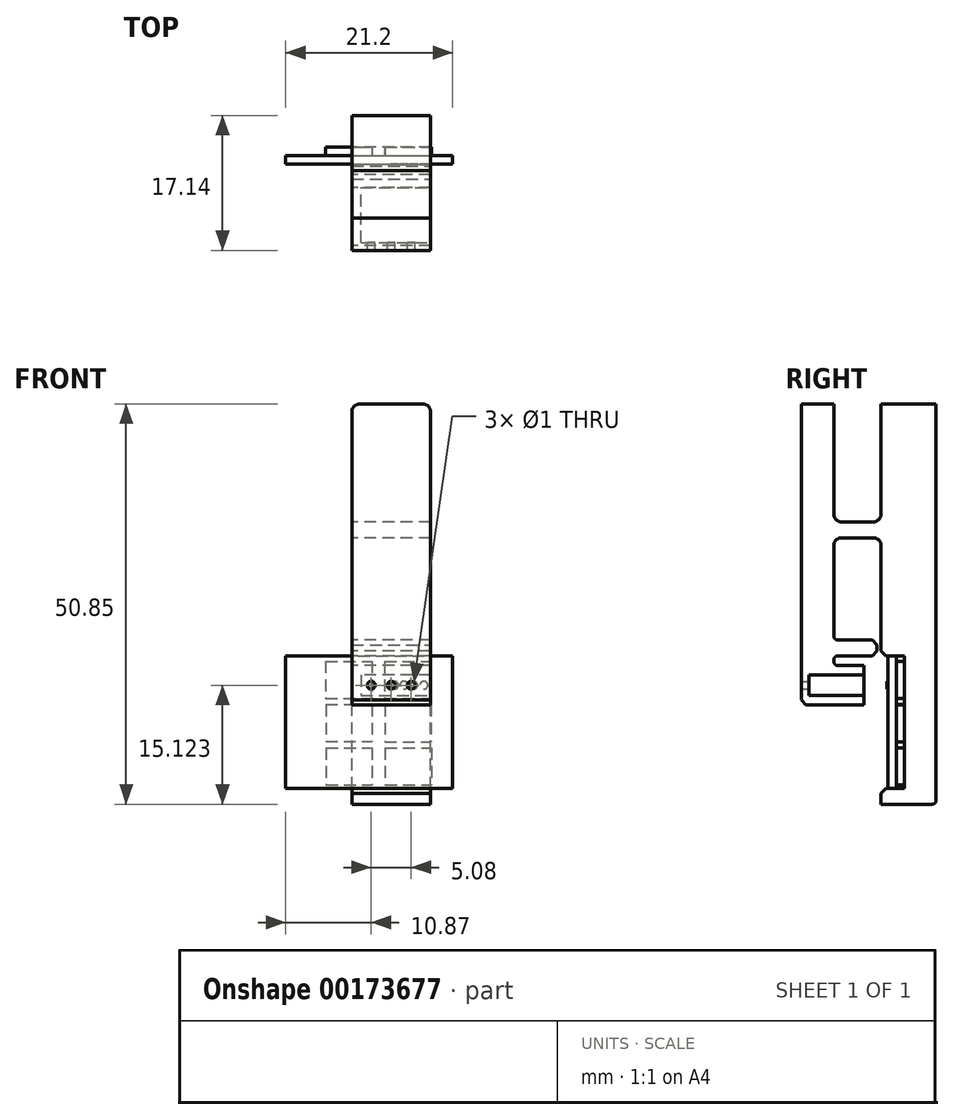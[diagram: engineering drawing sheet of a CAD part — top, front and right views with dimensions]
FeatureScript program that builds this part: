
annotation { "Feature Type Name" : "Feature", "Feature Type Description" : "" }
export const myFeature = defineFeature(function(context is Context, id is Id, definition is map)
    precondition{}
    {
        {
            var Q0;
            Q0=qCreatedBy(makeId("Front.planeOp"),FACE);
            var sketch = newSketch(context, id + "F0", { "sketchPlane" : qUnion([Q0])});
            skLineSegment(sketch, "E0.bottom", {"start": v(-8.41, 12.67) * mm, "end": v(12.79, 12.67) * mm});
            skLineSegment(sketch, "E0.top", {"start": v(-8.41, -4.18) * mm, "end": v(12.79, -4.18) * mm});
            skLineSegment(sketch, "E0.left", {"start": v(-8.41, 12.67) * mm, "end": v(-8.41, -4.18) * mm});
            skLineSegment(sketch, "E0.right", {"start": v(12.79, 12.67) * mm, "end": v(12.79, -4.18) * mm});
            skCircle(sketch, "E1", {"center": v(9.15, 8.94) * mm, "radius": 0.5 * mm});
            skCircle(sketch, "E2", {"center": v(7.85, 8.94) * mm, "radius": 0.5 * mm});
            skCircle(sketch, "E3", {"center": v(6.63, 8.94) * mm, "radius": 0.5 * mm});
            skCircle(sketch, "E4", {"center": v(5.4, 8.94) * mm, "radius": 0.5 * mm});
            skLineSegment(sketch, "E5.bottom", {"start": v(4.22, 0.96) * mm, "end": v(10.09, 0.96) * mm});
            skLineSegment(sketch, "E5.top", {"start": v(4.22, -3.74) * mm, "end": v(10.09, -3.74) * mm});
            skLineSegment(sketch, "E5.left", {"start": v(4.22, 0.96) * mm, "end": v(4.22, -3.74) * mm});
            skLineSegment(sketch, "E5.right", {"start": v(10.09, 0.96) * mm, "end": v(10.09, -3.74) * mm});
            skLineSegment(sketch, "E6.0.1.0", {"start": v(10.06, 6.46) * mm, "end": v(10.06, 1.76) * mm});
            skLineSegment(sketch, "E6.0.1.1", {"start": v(4.19, 6.46) * mm, "end": v(10.06, 6.46) * mm});
            skLineSegment(sketch, "E6.0.1.2", {"start": v(4.19, 6.46) * mm, "end": v(4.19, 1.76) * mm});
            skLineSegment(sketch, "E6.0.1.3", {"start": v(4.19, 1.76) * mm, "end": v(10.06, 1.76) * mm});
            skLineSegment(sketch, "E6.0.2.0", {"start": v(10.03, 11.96) * mm, "end": v(10.03, 7.26) * mm});
            skLineSegment(sketch, "E6.0.2.1", {"start": v(4.16, 11.96) * mm, "end": v(10.03, 11.96) * mm});
            skLineSegment(sketch, "E6.0.2.2", {"start": v(4.16, 11.96) * mm, "end": v(4.16, 7.26) * mm});
            skLineSegment(sketch, "E6.0.2.3", {"start": v(4.16, 7.26) * mm, "end": v(10.03, 7.26) * mm});
            skLineSegment(sketch, "E6.1.0.0", {"start": v(2.59, 0.98) * mm, "end": v(2.59, -3.72) * mm});
            skLineSegment(sketch, "E6.1.0.1", {"start": v(-3.28, 0.98) * mm, "end": v(2.59, 0.98) * mm});
            skLineSegment(sketch, "E6.1.0.2", {"start": v(-3.28, 0.98) * mm, "end": v(-3.28, -3.72) * mm});
            skLineSegment(sketch, "E6.1.0.3", {"start": v(-3.28, -3.72) * mm, "end": v(2.59, -3.72) * mm});
            skLineSegment(sketch, "E6.1.1.0", {"start": v(2.56, 6.48) * mm, "end": v(2.56, 1.78) * mm});
            skLineSegment(sketch, "E6.1.1.1", {"start": v(-3.31, 6.48) * mm, "end": v(2.56, 6.48) * mm});
            skLineSegment(sketch, "E6.1.1.2", {"start": v(-3.31, 6.48) * mm, "end": v(-3.31, 1.78) * mm});
            skLineSegment(sketch, "E6.1.1.3", {"start": v(-3.31, 1.78) * mm, "end": v(2.56, 1.78) * mm});
            skLineSegment(sketch, "E6.1.2.0", {"start": v(2.53, 11.98) * mm, "end": v(2.53, 7.28) * mm});
            skLineSegment(sketch, "E6.1.2.1", {"start": v(-3.34, 11.98) * mm, "end": v(2.53, 11.98) * mm});
            skLineSegment(sketch, "E6.1.2.2", {"start": v(-3.34, 11.98) * mm, "end": v(-3.34, 7.28) * mm});
            skLineSegment(sketch, "E6.1.2.3", {"start": v(-3.34, 7.28) * mm, "end": v(2.53, 7.28) * mm});
            skLineSegment(sketch, "E6.direction1", {"start": v(4.22, -3.74) * mm, "end": v(-3.28, -3.72) * mm, "construction": true});
            skLineSegment(sketch, "E6.direction2", {"start": v(4.22, -3.74) * mm, "end": v(4.19, 1.76) * mm, "construction": true});
            skSolve(sketch);
        }
        {
            var Q0;
            Q0=makeQuery(id+"F0.imprint","IMPRINT",FACE,{"disambiguationData":[TD([[makeQuery(id+"F0.imprint","IMPRINT",EDGE,{"derivedFrom":sQuery(id+"F0.wireOp",EDGE,"E0.bottom")}),-1.0]])]});
            var Q1;
            Q1=makeQuery(id+"F0.imprint","IMPRINT",FACE,{"disambiguationData":[TD([[makeQuery(id+"F0.imprint","IMPRINT",EDGE,{"derivedFrom":sQuery(id+"F0.wireOp",EDGE,"E6.1.2.0")}),-1.0]])]});
            var Q2;
            Q2=makeQuery(id+"F0.imprint","IMPRINT",FACE,{"disambiguationData":[TD([[makeQuery(id+"F0.imprint","IMPRINT",EDGE,{"derivedFrom":sQuery(id+"F0.wireOp",EDGE,"E1")}),-1.0]])]});
            var Q3;
            Q3=makeQuery(id+"F0.imprint","IMPRINT",FACE,{"disambiguationData":[TD([[makeQuery(id+"F0.imprint","IMPRINT",EDGE,{"derivedFrom":sQuery(id+"F0.wireOp",EDGE,"E6.1.1.0")}),-1.0]])]});
            var Q4;
            Q4=makeQuery(id+"F0.imprint","IMPRINT",FACE,{"disambiguationData":[TD([[makeQuery(id+"F0.imprint","IMPRINT",EDGE,{"derivedFrom":sQuery(id+"F0.wireOp",EDGE,"E6.0.1.0")}),-1.0]])]});
            var Q5;
            Q5=makeQuery(id+"F0.imprint","IMPRINT",FACE,{"disambiguationData":[TD([[makeQuery(id+"F0.imprint","IMPRINT",EDGE,{"derivedFrom":sQuery(id+"F0.wireOp",EDGE,"E6.1.0.0")}),-1.0]])]});
            var Q6;
            Q6=makeQuery(id+"F0.imprint","IMPRINT",FACE,{"disambiguationData":[TD([[makeQuery(id+"F0.imprint","IMPRINT",EDGE,{"derivedFrom":sQuery(id+"F0.wireOp",EDGE,"E5.bottom")}),-1.0]])]});
            extrude(context, id + "F1", {"entities" : qUnion([Q0, Q1, Q2, Q3, Q4, Q5, Q6]), "oppositeDirection" : true, "depth" : 1.08 * mm});
        }
        {
            var Q0;
            Q0=makeQuery(id+"F0.imprint","IMPRINT",FACE,{"disambiguationData":[TD([[makeQuery(id+"F0.imprint","IMPRINT",EDGE,{"derivedFrom":sQuery(id+"F0.wireOp",EDGE,"E6.1.0.0")}),-1.0]])]});
            var Q1;
            Q1=makeQuery(id+"F0.imprint","IMPRINT",FACE,{"disambiguationData":[TD([[makeQuery(id+"F0.imprint","IMPRINT",EDGE,{"derivedFrom":sQuery(id+"F0.wireOp",EDGE,"E6.1.1.0")}),-1.0]])]});
            var Q2;
            Q2=makeQuery(id+"F0.imprint","IMPRINT",FACE,{"disambiguationData":[TD([[makeQuery(id+"F0.imprint","IMPRINT",EDGE,{"derivedFrom":sQuery(id+"F0.wireOp",EDGE,"E6.1.2.0")}),-1.0]])]});
            var Q3;
            Q3=makeQuery(id+"F0.imprint","IMPRINT",FACE,{"disambiguationData":[TD([[makeQuery(id+"F0.imprint","IMPRINT",EDGE,{"derivedFrom":sQuery(id+"F0.wireOp",EDGE,"E5.bottom")}),-1.0]])]});
            var Q4;
            Q4=makeQuery(id+"F0.imprint","IMPRINT",FACE,{"disambiguationData":[TD([[makeQuery(id+"F0.imprint","IMPRINT",EDGE,{"derivedFrom":sQuery(id+"F0.wireOp",EDGE,"E6.0.1.0")}),-1.0]])]});
            var Q5;
            Q5=makeQuery(id+"F0.imprint","IMPRINT",FACE,{"disambiguationData":[TD([[makeQuery(id+"F0.imprint","IMPRINT",EDGE,{"derivedFrom":sQuery(id+"F0.wireOp",EDGE,"E1")}),-1.0]])]});
            var Q6;
            Q6=makeQuery(id+"F0.imprint","IMPRINT",FACE,{"disambiguationData":[TD([[makeQuery(id+"F0.imprint","IMPRINT",EDGE,{"derivedFrom":sQuery(id+"F0.wireOp",EDGE,"E4")}),1.0]])]});
            var Q7;
            Q7=makeQuery(id+"F0.imprint","IMPRINT",FACE,{"disambiguationData":[TD([[makeQuery(id+"F0.imprint","IMPRINT",EDGE,{"derivedFrom":sQuery(id+"F0.wireOp",EDGE,"E3")}),1.0]])]});
            var Q8;
            Q8=makeQuery(id+"F0.imprint","IMPRINT",FACE,{"disambiguationData":[TD([[makeQuery(id+"F0.imprint","IMPRINT",EDGE,{"derivedFrom":sQuery(id+"F0.wireOp",EDGE,"E2")}),1.0]])]});
            var Q9;
            Q9=makeQuery(id+"F0.imprint","IMPRINT",FACE,{"disambiguationData":[TD([[makeQuery(id+"F0.imprint","IMPRINT",EDGE,{"derivedFrom":sQuery(id+"F0.wireOp",EDGE,"E1")}),1.0]])]});
            extrude(context, id + "F2", {"entities" : qUnion([Q0, Q1, Q2, Q3, Q4, Q5, Q6, Q7, Q8, Q9]), "operationType" : NewBodyOperationType.ADD, "oppositeDirection" : true, "depth" : 2.14 * mm});
        }
        {
            var Q0;
            Q0=makeQuery(id+"F0.imprint","IMPRINT",FACE,{"disambiguationData":[TD([[makeQuery(id+"F0.imprint","IMPRINT",EDGE,{"derivedFrom":sQuery(id+"F0.wireOp",EDGE,"E4")}),1.0]])]});
            var Q1;
            Q1=makeQuery(id+"F0.imprint","IMPRINT",FACE,{"disambiguationData":[TD([[makeQuery(id+"F0.imprint","IMPRINT",EDGE,{"derivedFrom":sQuery(id+"F0.wireOp",EDGE,"E3")}),1.0]])]});
            var Q2;
            Q2=makeQuery(id+"F0.imprint","IMPRINT",FACE,{"disambiguationData":[TD([[makeQuery(id+"F0.imprint","IMPRINT",EDGE,{"derivedFrom":sQuery(id+"F0.wireOp",EDGE,"E2")}),1.0]])]});
            var Q3;
            Q3=makeQuery(id+"F0.imprint","IMPRINT",FACE,{"disambiguationData":[TD([[makeQuery(id+"F0.imprint","IMPRINT",EDGE,{"derivedFrom":sQuery(id+"F0.wireOp",EDGE,"E1")}),1.0]])]});
            extrude(context, id + "F3", {"entities" : qUnion([Q0, Q1, Q2, Q3]), "operationType" : NewBodyOperationType.ADD, "depth" : 0.1 * mm});
        }
        {
            var Q0;
            Q0=qCreatedBy(makeId("Right.planeOp"),FACE);
            var sketch = newSketch(context, id + "F4", { "sketchPlane" : qUnion([Q0])});
            skPoint(sketch, "E7.0", {"position": v(0, 8.94) * mm});
            skLineSegment(sketch, "E8.0", {"start": v(2.14, 11.98) * mm, "end": v(2.14, 7.28) * mm});
            skLineSegment(sketch, "E9.0", {"start": v(1.08, 12.67) * mm, "end": v(0, 12.67) * mm});
            skPoint(sketch, "E10.0", {"position": v(1.08, -4.18) * mm});
            skLineSegment(sketch, "E11", {"start": v(-0.86, -4.18) * mm, "end": v(2.14, -4.18) * mm});
            skLineSegment(sketch, "E12", {"start": v(2.14, -4.18) * mm, "end": v(2.14, 12.67) * mm});
            skLineSegment(sketch, "E13", {"start": v(2.14, 12.67) * mm, "end": v(-0.86, 12.67) * mm});
            skLineSegment(sketch, "E14", {"start": v(-0.86, 12.67) * mm, "end": v(-0.86, 27.67) * mm});
            skLineSegment(sketch, "E15", {"start": v(-0.86, 27.67) * mm, "end": v(-6.86, 27.67) * mm});
            skLineSegment(sketch, "E16", {"start": v(-6.86, 27.67) * mm, "end": v(-6.86, 14.67) * mm});
            skLineSegment(sketch, "E17", {"start": v(-6.86, 14.67) * mm, "end": v(-1.36, 14.67) * mm});
            skLineSegment(sketch, "E18", {"start": v(-1.36, 14.67) * mm, "end": v(-1.36, 12.67) * mm});
            skLineSegment(sketch, "E19", {"start": v(-1.36, 12.67) * mm, "end": v(-6.86, 12.67) * mm});
            skLineSegment(sketch, "E20", {"start": v(-6.86, 12.67) * mm, "end": v(-6.86, 11.44) * mm});
            skLineSegment(sketch, "E21", {"start": v(-6.86, 11.44) * mm, "end": v(-3, 11.44) * mm});
            skLineSegment(sketch, "E22", {"start": v(-3, 11.44) * mm, "end": v(-3, 6.44) * mm});
            skLineSegment(sketch, "E23", {"start": v(-3, 6.44) * mm, "end": v(-11, 6.44) * mm});
            skLineSegment(sketch, "E24", {"start": v(-11, 6.44) * mm, "end": v(-11, 44.67) * mm});
            skLineSegment(sketch, "E25", {"start": v(-11, 44.67) * mm, "end": v(-6.86, 44.67) * mm});
            skLineSegment(sketch, "E26", {"start": v(-6.86, 44.67) * mm, "end": v(-6.86, 29.67) * mm});
            skLineSegment(sketch, "E27", {"start": v(-6.86, 29.67) * mm, "end": v(-0.86, 29.67) * mm});
            skLineSegment(sketch, "E28", {"start": v(-0.86, 29.67) * mm, "end": v(-0.86, 44.67) * mm});
            skLineSegment(sketch, "E29", {"start": v(-0.86, 44.67) * mm, "end": v(6.14, 44.67) * mm});
            skLineSegment(sketch, "E30", {"start": v(6.14, 44.67) * mm, "end": v(6.14, -6.18) * mm});
            skLineSegment(sketch, "E31", {"start": v(6.14, -6.18) * mm, "end": v(-0.86, -6.18) * mm});
            skLineSegment(sketch, "E32", {"start": v(-0.86, -6.18) * mm, "end": v(-0.86, -4.18) * mm});
            skLineSegment(sketch, "E33", {"start": v(0, 8.94) * mm, "end": v(-3, 8.94) * mm, "construction": true});
            skSolve(sketch);
        }
        {
            var Q0;
            Q0 = qSketchRegion(id + "F4", true);
            extrude(context, id + "F5", {"entities" : qUnion([Q0]), "depth" : 10 * mm});
        }
        {
            var Q0;
            Q0=makeQuery(id+"F5.opExtrude","SWEPT_FACE",FACE,{"disambiguationData":[OSD([sQuery(id+"F4.wireOp",EDGE,"E22")])]});
            var sketch = newSketch(context, id + "F6", { "sketchPlane" : qUnion([Q0])});
            skLineSegment(sketch, "E34", {"start": v(-10, 8.94) * mm, "end": v(0, 8.94) * mm, "construction": true});
            skLineSegment(sketch, "E35", {"start": v(-5, 6.44) * mm, "end": v(-5, 11.44) * mm, "construction": true});
            skLineSegment(sketch, "E36.bottom", {"start": v(-1.14, 10.22) * mm, "end": v(-8.86, 10.22) * mm});
            skLineSegment(sketch, "E36.top", {"start": v(-1.14, 7.67) * mm, "end": v(-8.86, 7.67) * mm});
            skLineSegment(sketch, "E36.left", {"start": v(-1.14, 10.22) * mm, "end": v(-1.14, 7.67) * mm});
            skLineSegment(sketch, "E36.right", {"start": v(-8.86, 10.22) * mm, "end": v(-8.86, 7.67) * mm});
            skPoint(sketch, "E36.middle", {"position": v(-5, 8.94) * mm});
            skCircle(sketch, "E37", {"center": v(-5, 8.94) * mm, "radius": 0.5 * mm});
            skCircle(sketch, "E38", {"center": v(-7.54, 8.94) * mm, "radius": 0.5 * mm});
            skCircle(sketch, "E39", {"center": v(-2.46, 8.94) * mm, "radius": 0.5 * mm});
            skLineSegment(sketch, "E40", {"start": v(-8.86, 7.67) * mm, "end": v(-10, 7.67) * mm});
            skLineSegment(sketch, "E41", {"start": v(-10, 7.67) * mm, "end": v(-10, 10.22) * mm});
            skLineSegment(sketch, "E42", {"start": v(-10, 10.22) * mm, "end": v(-8.86, 10.22) * mm});
            skSolve(sketch);
        }
        {
            var Q0;
            Q0 = qSketchRegion(id + "F6", true);
            var Q1;
            Q1=makeQuery(id+"F6.imprint","IMPRINT",FACE,{"disambiguationData":[TD([[makeQuery(id+"F6.imprint","IMPRINT",EDGE,{"derivedFrom":sQuery(id+"F6.wireOp",EDGE,"E38")}),1.0]])]});
            var Q2;
            Q2=makeQuery(id+"F6.imprint","IMPRINT",FACE,{"disambiguationData":[TD([[makeQuery(id+"F6.imprint","IMPRINT",EDGE,{"derivedFrom":sQuery(id+"F6.wireOp",EDGE,"E37")}),1.0]])]});
            var Q3;
            Q3=makeQuery(id+"F6.imprint","IMPRINT",FACE,{"disambiguationData":[TD([[makeQuery(id+"F6.imprint","IMPRINT",EDGE,{"derivedFrom":sQuery(id+"F6.wireOp",EDGE,"E39")}),1.0]])]});
            extrude(context, id + "F7", {"entities" : qUnion([Q0, Q1, Q2, Q3]), "operationType" : NewBodyOperationType.REMOVE, "oppositeDirection" : true, "depth" : 7 * mm});
        }
        {
            var Q0;
            Q0=makeQuery(id+"F6.imprint","IMPRINT",FACE,{"disambiguationData":[TD([[makeQuery(id+"F6.imprint","IMPRINT",EDGE,{"derivedFrom":sQuery(id+"F6.wireOp",EDGE,"E39")}),1.0]])]});
            var Q1;
            Q1=makeQuery(id+"F6.imprint","IMPRINT",FACE,{"disambiguationData":[TD([[makeQuery(id+"F6.imprint","IMPRINT",EDGE,{"derivedFrom":sQuery(id+"F6.wireOp",EDGE,"E37")}),1.0]])]});
            var Q2;
            Q2=makeQuery(id+"F6.imprint","IMPRINT",FACE,{"disambiguationData":[TD([[makeQuery(id+"F6.imprint","IMPRINT",EDGE,{"derivedFrom":sQuery(id+"F6.wireOp",EDGE,"E38")}),1.0]])]});
            extrude(context, id + "F8", {"entities" : qUnion([Q0, Q1, Q2]), "operationType" : NewBodyOperationType.REMOVE, "endBound" : BoundingType.THROUGH_ALL, "oppositeDirection" : true, "depth" : 25 * mm});
        }
        {
            var Q0;
            Q0=makeQuery(id+"F5.opExtrude","SWEPT_EDGE",EDGE,{"disambiguationData":[OSD([sQuery(id+"F4.wireOp",EDGE,"E27"),sQuery(id+"F4.wireOp",EDGE,"E28")])]});
            var Q1;
            Q1=makeQuery(id+"F5.opExtrude","SWEPT_EDGE",EDGE,{"disambiguationData":[OSD([sQuery(id+"F4.wireOp",EDGE,"E14"),sQuery(id+"F4.wireOp",EDGE,"E15")])]});
            var Q2;
            Q2=makeQuery(id+"F5.opExtrude","SWEPT_EDGE",EDGE,{"disambiguationData":[OSD([sQuery(id+"F4.wireOp",EDGE,"E15"),sQuery(id+"F4.wireOp",EDGE,"E16")])]});
            var Q3;
            Q3=makeQuery(id+"F5.opExtrude","SWEPT_EDGE",EDGE,{"disambiguationData":[OSD([sQuery(id+"F4.wireOp",EDGE,"E26"),sQuery(id+"F4.wireOp",EDGE,"E27")])]});
            var Q4;
            Q4=makeQuery(id+"F5.opExtrude","CAP_EDGE",EDGE,{"disambiguationData":[OSD([sQuery(id+"F4.wireOp",EDGE,"E25")])],"isStart":false});
            var Q5;
            Q5=makeQuery(id+"F5.opExtrude","CAP_EDGE",EDGE,{"disambiguationData":[OSD([sQuery(id+"F4.wireOp",EDGE,"E25")])],"isStart":true});
            var Q6;
            Q6=makeQuery(id+"F5.opExtrude","CAP_EDGE",EDGE,{"disambiguationData":[OSD([sQuery(id+"F4.wireOp",EDGE,"E29")])],"isStart":true});
            var Q7;
            Q7=makeQuery(id+"F5.opExtrude","CAP_EDGE",EDGE,{"disambiguationData":[OSD([sQuery(id+"F4.wireOp",EDGE,"E29")])],"isStart":false});
            fillet(context, id + "F9", {"entities" : qUnion([Q0, Q1, Q2, Q3, Q4, Q5, Q6, Q7]), "radius" : 1 * mm, "tangentPropagation" : true, "allowEdgeOverflow" : false});
        }
        {
            var Q0;
            Q0=makeQuery(id+"F5.opExtrude","SWEPT_EDGE",EDGE,{"disambiguationData":[OSD([sQuery(id+"F4.wireOp",EDGE,"E23"),sQuery(id+"F4.wireOp",EDGE,"E24")])]});
            var Q1;
            Q1=makeQuery(id+"F5.opExtrude","SWEPT_EDGE",EDGE,{"disambiguationData":[OSD([sQuery(id+"F4.wireOp",EDGE,"E11"),sQuery(id+"F4.wireOp",EDGE,"E32")])]});
            var Q2;
            Q2=makeQuery(id+"F5.opExtrude","SWEPT_EDGE",EDGE,{"disambiguationData":[OSD([sQuery(id+"F4.wireOp",EDGE,"E13"),sQuery(id+"F4.wireOp",EDGE,"E14")])]});
            var Q3;
            Q3=makeQuery(id+"F5.opExtrude","SWEPT_EDGE",EDGE,{"disambiguationData":[OSD([sQuery(id+"F4.wireOp",EDGE,"E18"),sQuery(id+"F4.wireOp",EDGE,"E19")])]});
            var Q4;
            Q4=makeQuery(id+"F5.opExtrude","SWEPT_EDGE",EDGE,{"disambiguationData":[OSD([sQuery(id+"F4.wireOp",EDGE,"E17"),sQuery(id+"F4.wireOp",EDGE,"E18")])]});
            chamfer(context, id + "F10", {"entities" : qUnion([Q0, Q1, Q2, Q3, Q4]), "width" : 0.6 * mm, "tangentPropagation" : true});
        }
        {
            var Q0;
            Q0=makeQuery(id+"F5.opExtrude","SWEPT_EDGE",EDGE,{"disambiguationData":[OSD([sQuery(id+"F4.wireOp",EDGE,"E19"),sQuery(id+"F4.wireOp",EDGE,"E20")])]});
            var Q1;
            Q1=makeQuery(id+"F5.opExtrude","SWEPT_EDGE",EDGE,{"disambiguationData":[OSD([sQuery(id+"F4.wireOp",EDGE,"E16"),sQuery(id+"F4.wireOp",EDGE,"E17")])]});
            var Q2;
            Q2=makeQuery(id+"F5.opExtrude","SWEPT_EDGE",EDGE,{"disambiguationData":[OSD([sQuery(id+"F4.wireOp",EDGE,"E20"),sQuery(id+"F4.wireOp",EDGE,"E21")])]});
            var Q3;
            Q3=makeQuery(id+"F5.opExtrude","SWEPT_EDGE",EDGE,{"disambiguationData":[OSD([sQuery(id+"F4.wireOp",EDGE,"E30"),sQuery(id+"F4.wireOp",EDGE,"E31")])]});
            fillet(context, id + "F11", {"entities" : qUnion([Q0, Q1, Q2, Q3]), "radius" : 0.5 * mm, "tangentPropagation" : true, "allowEdgeOverflow" : false});
        }
    });
